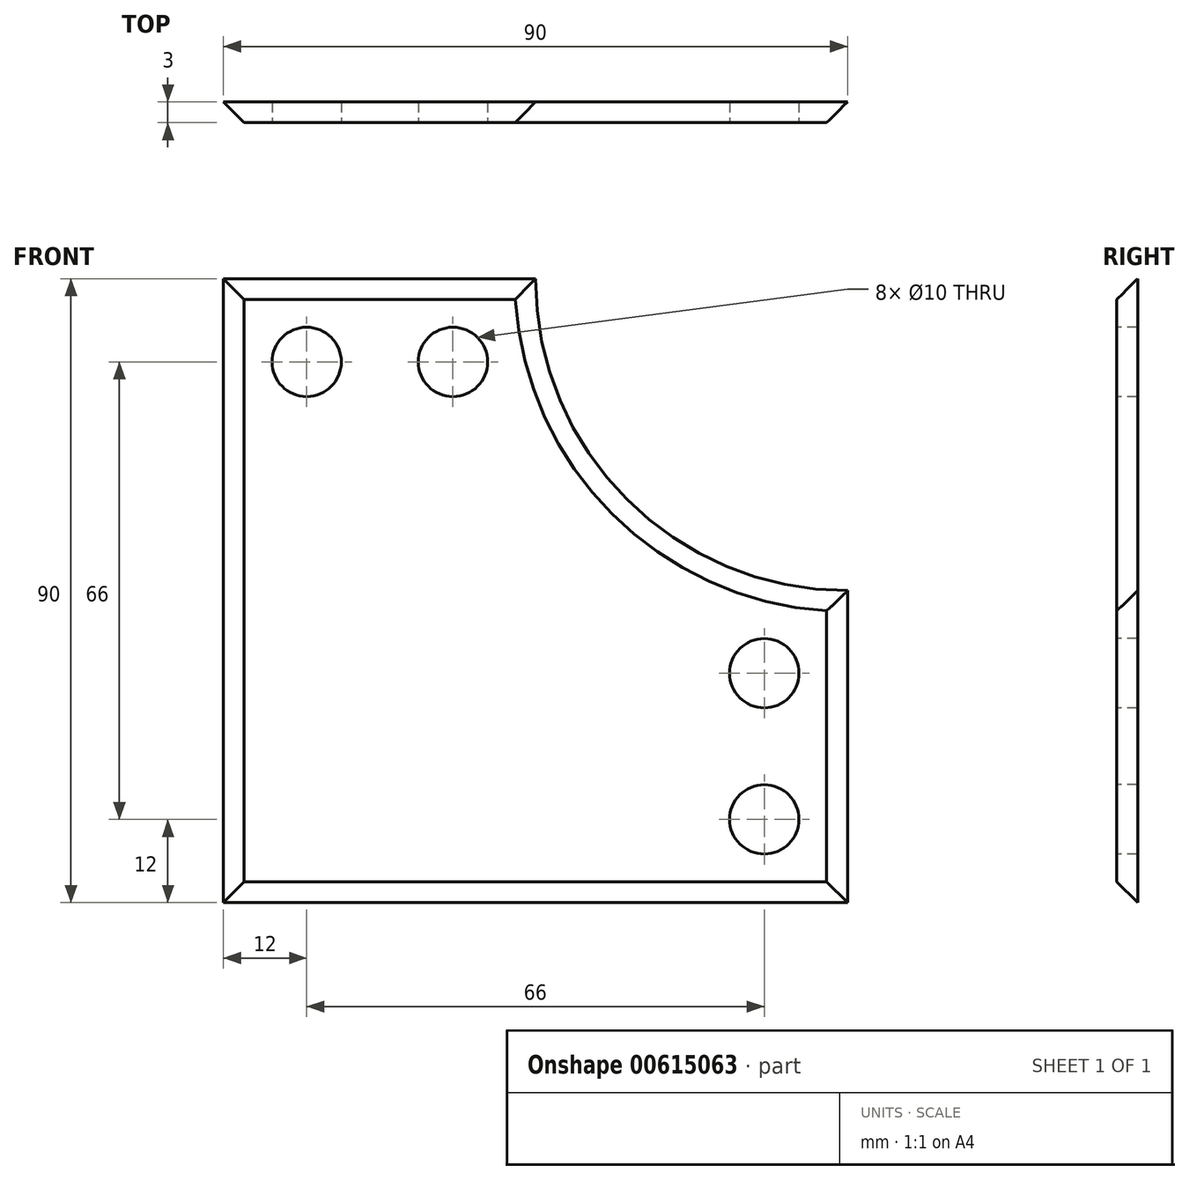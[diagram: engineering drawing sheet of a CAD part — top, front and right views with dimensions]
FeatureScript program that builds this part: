
annotation { "Feature Type Name" : "Feature", "Feature Type Description" : "" }
export const myFeature = defineFeature(function(context is Context, id is Id, definition is map)
    precondition{}
    {
        {
            var Q0;
            Q0=qCreatedBy(makeId("Front.planeOp"),FACE);
            var sketch = newSketch(context, id + "F0", { "sketchPlane" : qUnion([Q0])});
            skLineSegment(sketch, "E0", {"start": v(0, 0) * mm, "end": v(90, 0) * mm});
            skLineSegment(sketch, "E1", {"start": v(90, 0) * mm, "end": v(90, 45) * mm});
            skLineSegment(sketch, "E2", {"start": v(0, 0) * mm, "end": v(0, 90) * mm});
            skLineSegment(sketch, "E3", {"start": v(0, 90) * mm, "end": v(45, 90) * mm});
            skArc(sketch, "E4", {"start": v(45, 90) * mm, "mid": v(58.18, 58.18) * mm, "end": v(90, 45) * mm});
            skSolve(sketch);
        }
        {
            var Q0;
            Q0 = qSketchRegion(id + "F0", true);
            extrude(context, id + "F1", {"entities" : qUnion([Q0]), "depth" : 3 * mm, "offsetDistance" : 25 * mm});
        }
        {
            var Q0;
            Q0=makeQuery(id+"F1.opExtrude","CAP_EDGE",EDGE,{"disambiguationData":[OSD([sQuery(id+"F0.wireOp",EDGE,"E3")])],"isStart":false});
            var Q1;
            Q1=makeQuery(id+"F1.opExtrude","CAP_FACE",FACE,{"disambiguationData":[OSD([sQuery(id+"F0.wireOp",EDGE,"E0"),sQuery(id+"F0.wireOp",EDGE,"E1"),sQuery(id+"F0.wireOp",EDGE,"E2"),sQuery(id+"F0.wireOp",EDGE,"E3"),sQuery(id+"F0.wireOp",EDGE,"E4")])],"isStart":false});
            chamfer(context, id + "F2", {"entities" : qUnion([Q0, Q1]), "width" : 3 * mm, "tangentPropagation" : true});
        }
        {
            var Q0;
            Q0=makeQuery(id+"F1.opExtrude","CAP_FACE",FACE,{"disambiguationData":[OSD([sQuery(id+"F0.wireOp",EDGE,"E0"),sQuery(id+"F0.wireOp",EDGE,"E1"),sQuery(id+"F0.wireOp",EDGE,"E2"),sQuery(id+"F0.wireOp",EDGE,"E3"),sQuery(id+"F0.wireOp",EDGE,"E4")])],"isStart":false});
            var sketch = newSketch(context, id + "F3", { "sketchPlane" : qUnion([Q0])});
            skPoint(sketch, "E5", {"position": v(0, 0) * mm});
            skPoint(sketch, "E6", {"position": v(90, 90) * mm});
            skLineSegment(sketch, "E7", {"start": v(0, 0) * mm, "end": v(90, 90) * mm, "construction": true});
            skPoint(sketch, "E8", {"position": v(12, 78) * mm});
            skLineSegment(sketch, "E9", {"start": v(22.55, 87) * mm, "end": v(22.55, 3) * mm, "construction": true});
            skPoint(sketch, "E10.MirrorP", {"position": v(33.1, 78) * mm});
            skPoint(sketch, "E11.MirrorP", {"position": v(78, 33.1) * mm});
            skPoint(sketch, "E12.MirrorP", {"position": v(78, 12) * mm});
            skSolve(sketch);
        }
        {
            var Q0;
            Q0=sQuery(id+"F3.wireOp",VERTEX,"E8");
            var Q1;
            Q1=sQuery(id+"F3.wireOp",VERTEX,"E10.MirrorP");
            var Q2;
            Q2=sQuery(id+"F3.wireOp",VERTEX,"E11.MirrorP");
            var Q3;
            Q3=sQuery(id+"F3.wireOp",VERTEX,"E12.MirrorP");
            var Q4;
            Q4=makeQuery(id+"F1.opExtrude","SWEPT_BODY",BODY,{"disambiguationData":[OSD([sQuery(id+"F0.wireOp",EDGE,"E0"),sQuery(id+"F0.wireOp",EDGE,"E1"),sQuery(id+"F0.wireOp",EDGE,"E2"),sQuery(id+"F0.wireOp",EDGE,"E3"),sQuery(id+"F0.wireOp",EDGE,"E4")])]});
            hole(context, id + "F4", {"style" : HoleStyle.SIMPLE, "endStyle" : HoleEndStyle.BLIND, "holeDiameter" : 10 * mm, "majorDiameter" : 5 * mm, "holeDepth" : 9 * mm, "isTappedThrough" : true, "tappedDepth" : 5 * mm, "tapClearance" : 0, "locations" : qUnion([Q0, Q1, Q2, Q3]), "scope" : qUnion([Q4])});
        }
    });
